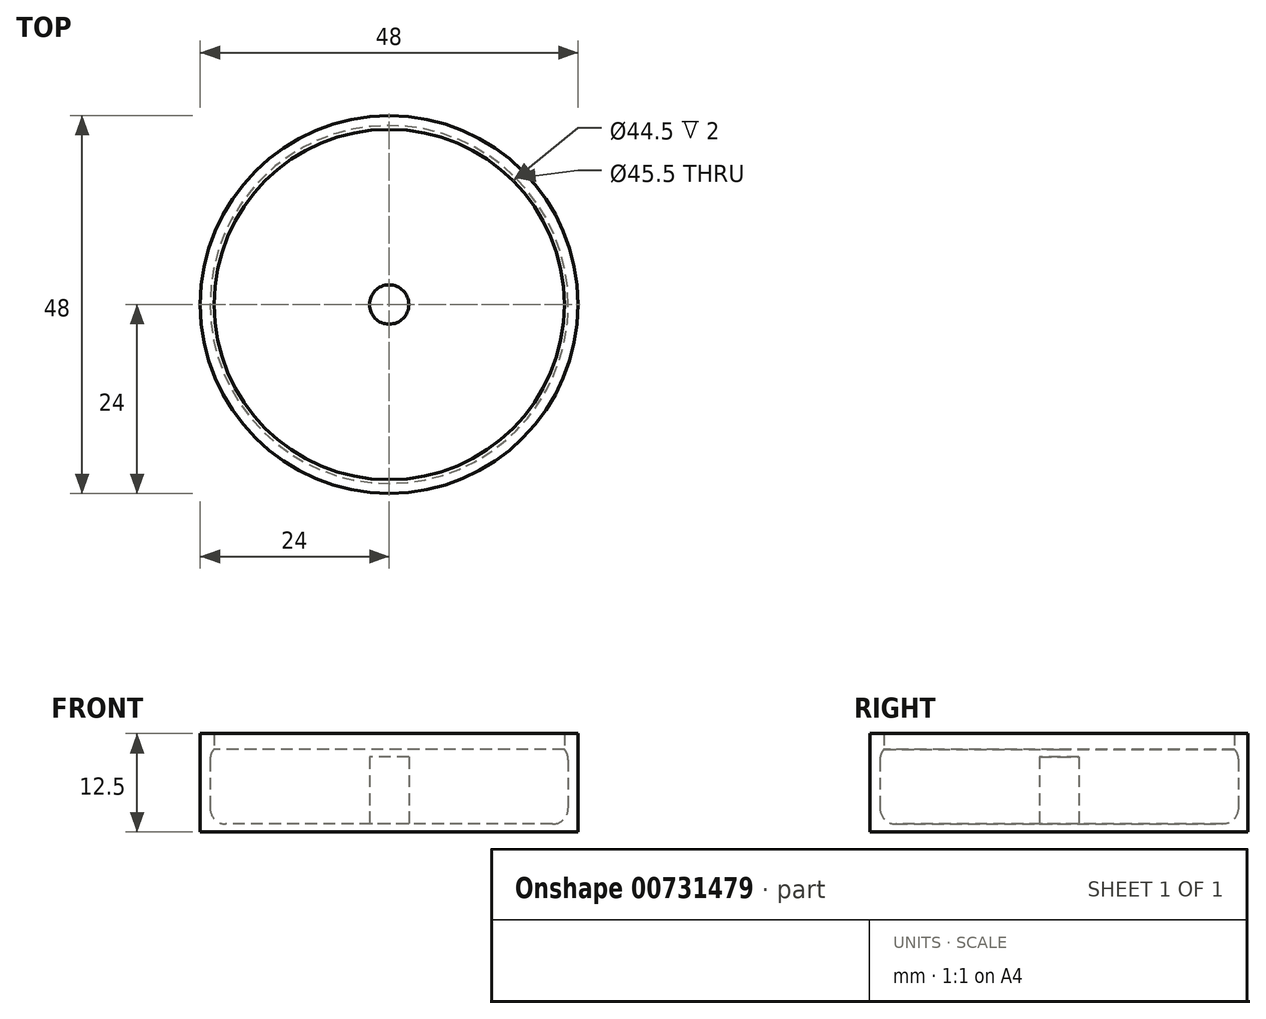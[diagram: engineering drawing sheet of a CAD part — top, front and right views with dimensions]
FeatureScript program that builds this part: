
annotation { "Feature Type Name" : "Feature", "Feature Type Description" : "" }
export const myFeature = defineFeature(function(context is Context, id is Id, definition is map)
    precondition{}
    {
        {
            var Q0;
            Q0=qCreatedBy(makeId("Top.planeOp"),FACE);
            var sketch = newSketch(context, id + "F0", { "sketchPlane" : qUnion([Q0])});
            skCircle(sketch, "E0", {"center": v(0, 0) * mm, "radius": 24 * mm});
            skSolve(sketch);
        }
        {
            var Q0;
            Q0 = qSketchRegion(id + "F0", true);
            extrude(context, id + "F1", {"entities" : qUnion([Q0]), "depth" : 12 * mm, "offsetDistance" : 25 * mm});
        }
        {
            var Q0;
            Q0=qCreatedBy(makeId("Top.planeOp"),FACE);
            var sketch = newSketch(context, id + "F2", { "sketchPlane" : qUnion([Q0])});
            skCircle(sketch, "E1", {"center": v(0, 0) * mm, "radius": 22.25 * mm});
            skSolve(sketch);
        }
        {
            var Q0;
            Q0 = qSketchRegion(id + "F2", true);
            extrude(context, id + "F3", {"entities" : qUnion([Q0]), "operationType" : NewBodyOperationType.REMOVE, "depth" : 13 * mm, "offsetDistance" : 25 * mm});
        }
        {
            var Q0;
            Q0=qCreatedBy(makeId("Top.planeOp"),FACE);
            var sketch = newSketch(context, id + "F4", { "sketchPlane" : qUnion([Q0])});
            skCircle(sketch, "E2", {"center": v(0, 0) * mm, "radius": 2.5 * mm});
            skSolve(sketch);
        }
        {
            var Q0;
            Q0=qCreatedBy(makeId("Top.planeOp"),FACE);
            var sketch = newSketch(context, id + "F5", { "sketchPlane" : qUnion([Q0])});
            skCircle(sketch, "E3", {"center": v(0, 0) * mm, "radius": 22.75 * mm});
            skSolve(sketch);
        }
        {
            var Q0;
            Q0 = qSketchRegion(id + "F5", true);
            extrude(context, id + "F6", {"entities" : qUnion([Q0]), "operationType" : NewBodyOperationType.REMOVE, "depth" : 10 * mm, "offsetDistance" : 25 * mm});
        }
        {
            var Q0;
            Q0 = qSketchRegion(id + "F4", true);
            extrude(context, id + "F7", {"entities" : qUnion([Q0]), "depth" : 9 * mm, "offsetDistance" : 25 * mm});
        }
        {
            var Q0;
            Q0=qCreatedBy(makeId("Top.planeOp"),FACE);
            var sketch = newSketch(context, id + "F8", { "sketchPlane" : qUnion([Q0])});
            skCircle(sketch, "E4", {"center": v(0, 0) * mm, "radius": 24 * mm});
            skSolve(sketch);
        }
        {
            var Q0;
            Q0 = qSketchRegion(id + "F8", true);
            extrude(context, id + "F9", {"entities" : qUnion([Q0]), "operationType" : NewBodyOperationType.ADD, "endBound" : BoundingType.SYMMETRIC, "oppositeDirection" : true, "depth" : 1 * mm, "offsetDistance" : 25 * mm});
        }
        {
            var Q0;
            Q0=makeQuery(id+"F6.boolean.opBoolean","COPY",FACE,{"derivedFrom":makeQuery(id+"F6.opExtrude","SWEPT_FACE",FACE,{"disambiguationData":[OSD([sQuery(id+"F5.wireOp",EDGE,"E3")])]})});
            fillet(context, id + "F10", {"entities" : qUnion([Q0]), "radius" : 2 * mm, "tangentPropagation" : true, "allowEdgeOverflow" : false});
        }
    });
